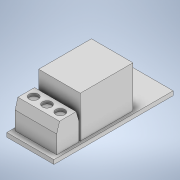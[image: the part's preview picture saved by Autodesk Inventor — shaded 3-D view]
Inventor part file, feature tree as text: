
AUTODESK INVENTOR PART (.ipt)
format: ipt  version: 2020.2 (Build 242310000, 310)  size: 143,872 bytes
history: native  units: mm
features: extrude x4, sketch x4, chamfer x2
ambient origin geometry x8: Origin, YZ Plane, XZ Plane, XY Plane, X Axis, Y Axis, Z Axis, Center Point
bodies: Solid1 (feature_tree)
feature tree (10):
  extrude  "Extrusion1"  Depth=17.0mm
  extrude  "Extrusion2"  Depth=19.0mm
  extrude  "Extrusion3"  Depth=15.0mm
  chamfer  "Chamfer1"  Distance=15.0mm
  chamfer  "Chamfer2"  Distance=15.0mm
  extrude  "Extrusion4"  Depth=8.0mm
  sketch  "Sketch1"  dims[d0=43.0mm d1=17.0mm]
  sketch  "Sketch2"  dims[d2=1.5mm d3=0.0mm d4=19.0mm]
  sketch  "Sketch3"  dims[d5=15.0mm d6=7.5mm]
  sketch  "Sketch4"  dims[d8=10.5mm d9=15.0mm d10=0.0mm d11=15.0mm d12=8.0mm d13=0.5mm d14=7.5mm d15=10.0mm d16=0.0mm d17=1.0mm d18=3.5mm d19=45.0deg d20=1.0mm d21=3.5mm d22=45.0deg d23=3.3mm d24=2.7mm d25=30.0mm d27=4.8mm d28=10.0mm d30=10.0mm d32=6.0mm d33=3.0mm d34=1.0mm d35=0.0mm]
